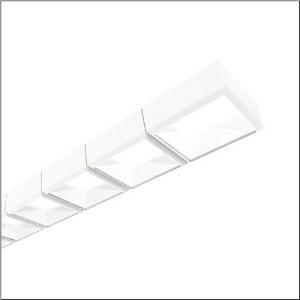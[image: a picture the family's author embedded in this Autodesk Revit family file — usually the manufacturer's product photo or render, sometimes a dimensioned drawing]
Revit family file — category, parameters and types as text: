
# Revit family: scriptus_r__11_5mz214d0twa_b782
name_source: partatom
category: Lighting Fixtures
units: mm (PartAtom-declared; Revit-internal decimal feet)

## family parameters
Cut with Voids When Loaded = No
Host = Face
Light Source = No
Part Type = Normal
Room Calculation Point = No
Round Connector Dimension = Use Diameter
Shared = No

## types (1)
- --- (1 x LED 3000K+6500K / CRI = 80 (unbekannt), 3600 lm, 3000K)
    Apparent Load = 53 VA
    CIE Flux Codes = 82 95 99 100 100
    Color Rendering = 80
    Color Temperature = 3000K
    Default Elevation = 1800 mm
    Description = Scriptus® 11, office luminaire, primary optical cover: lenses, CAT 2 (L<= 3000cd/m²), light emission: direct distribution, primary light characteristic: symmetric, installation type: surface-mounted, LED, rated luminous flux: 7.190lm, luminous efficacy: 137lm/W, light colour: 8tw, colour temperature: 3000..6500K, control gear: DALI, with terminal, 5-pole, mains connection: 230V, AC, 50Hz, rated input power: 53W, housing, luminaire housing, of aluminium, traffic white (RAL 9016), length: 3.088mm, width: 114mm, height: 57mm, protection rating (complete): IP20, insulation class (complete): insulation class I (protective earthing), certification: CE, protection symbol: F, permissible operating ambient temperature: 0..+35°C, standard: EN 50419, packaging unit: 1 piece
    Height = 57 mm
    Lamp = 1 x LED 3000K+6500K / CRI >= 80 (unbekannt)
    Lamp Light Flux = 3600 lm
    Lamp count = 1
    Length = 3088 mm
    Luminous efficacy = 137 lm/W
    Manufacturer = Siteco
    ModVariant = No
    Model = 5MZ214D0TWA
    Mounting Place = Ceiling
    Mounting Type = Surface mounted
    Number of Poles = 1
    OnlyDefault = Yes
    Power Factor = 1
    Product Name = Scriptus® 11
    Product group = office luminaire | ceiling mounted
    ProductGroupID = 303
    Protection Class = Protection class I
    Protection Degree = IP 20
    RLX_Detail_Level = 1
    RLX_Emergency_Light_Flux = 0 lm
    RLX_Emergency_Type = 0
    RLX_Emergency_Type_DB = No
    RlxData = <blob elided: 30417 chars, md5=a11394b1>
    Socket = socket
    Standby Power = 0 W
    System Light Flux = 7200 lm
    System Power = 53 W
    Type Comments = individual setting: colour temperature 6500K
    Type Image = l_1004833.jpg
    URL = http://relux.com
    VarID = @adj_220101
    Voltage = 0 V
    Weight = 0.00 kg
    Width = 114 mm

## geometry (parser evidence)
native form markers: Blend x4, Sweep x14
no freeform markers — native parametric forms only
